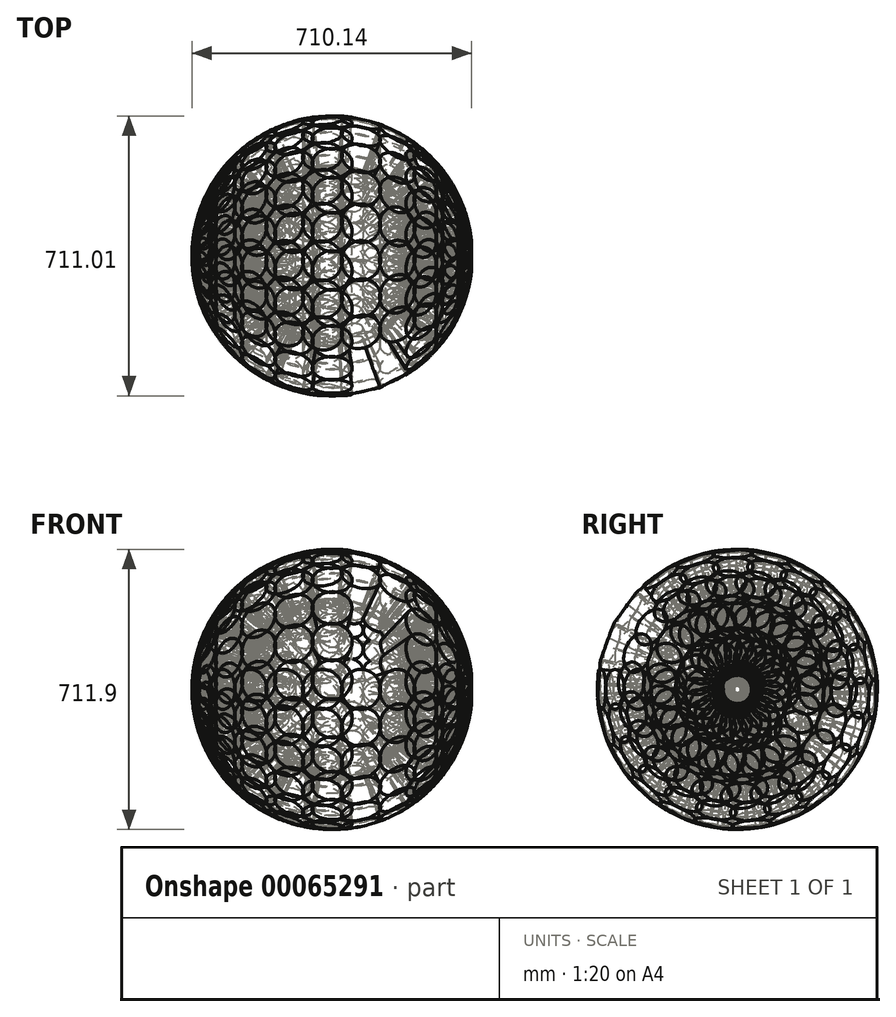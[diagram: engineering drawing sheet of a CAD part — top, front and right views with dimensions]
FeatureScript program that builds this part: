
annotation { "Feature Type Name" : "Feature", "Feature Type Description" : "" }
export const myFeature = defineFeature(function(context is Context, id is Id, definition is map)
    precondition{}
    {
        {
            var Q0;
            Q0=qCreatedBy(makeId("Top.planeOp"),FACE);
            var sketch = newSketch(context, id + "F4", { "sketchPlane" : qUnion([Q0])});
            skLineSegment(sketch, "E0", {"start": v(0, 228.6) * mm, "end": v(0, 352.43) * mm});
            skLineSegment(sketch, "E1", {"start": v(0, 352.43) * mm, "end": v(50.8, 352.43) * mm});
            skLineSegment(sketch, "E2", {"start": v(50.8, 352.43) * mm, "end": v(31.75, 228.6) * mm});
            skLineSegment(sketch, "E3", {"start": v(31.75, 228.6) * mm, "end": v(0, 228.6) * mm});
            skLineSegment(sketch, "E4", {"start": v(31.75, 228.6) * mm, "end": v(31.75, 352.43) * mm, "construction": true});
            skSolve(sketch);
        }
        {
            var Q0;
            Q0=makeQuery(id+"F4.imprint","IMPRINT",FACE,{"disambiguationData":[TD([[makeQuery(id+"F4.imprint","IMPRINT",EDGE,{"derivedFrom":sQuery(id+"F4.wireOp",EDGE,"E0")}),-1.0]])]});
            var Q1;
            Q1=sQuery(id+"F4.wireOp",EDGE,"E0");
            var Q2;
            Q2=sQuery(id+"F4.wireOp",EDGE,"E0");
            revolve(context, id + "F5", {"entities" : qUnion([Q0]), "surfaceEntities" : qUnion([Q1]), "axis" : qUnion([Q2]), "revolveType" : RevolveType.FULL});
        }
        {
            var Q0;
            Q0=qCreatedBy(makeId("Top.planeOp"),FACE);
            var sketch = newSketch(context, id + "F0", { "sketchPlane" : qUnion([Q0])});
            skCircle(sketch, "E5", {"center": v(0, 0) * mm, "radius": 228.6 * mm});
            skSolve(sketch);
        }
        {
            var Q0;
            Q0=makeQuery(id+"F5.opRevolve","SWEPT_BODY",BODY,{"disambiguationData":[OSD([sQuery(id+"F4.wireOp",EDGE,"E0"),sQuery(id+"F4.wireOp",EDGE,"E1"),sQuery(id+"F4.wireOp",EDGE,"E2"),sQuery(id+"F4.wireOp",EDGE,"E3")])]});
            var Q1;
            Q1=sQuery(id+"F0.wireOp",EDGE,"E5");
            circularPattern(context, id + "F1", {"operationType" : NewBodyOperationType.ADD, "entities" : qUnion([Q0]), "axis" : qUnion([Q1]), "angle" : 16 * degree, "instanceCount" : 21});
        }
        {
            var Q0;
            Q0=qCreatedBy(makeId("Right.planeOp"),FACE);
            var sketch = newSketch(context, id + "F2", { "sketchPlane" : qUnion([Q0])});
            skCircle(sketch, "E6", {"center": v(0, 0) * mm, "radius": 228.6 * mm});
            skSolve(sketch);
        }
        {
            var Q0;
            Q0=makeQuery(id+"F5.opRevolve","SWEPT_BODY",BODY,{"disambiguationData":[OSD([sQuery(id+"F4.wireOp",EDGE,"E0"),sQuery(id+"F4.wireOp",EDGE,"E1"),sQuery(id+"F4.wireOp",EDGE,"E2"),sQuery(id+"F4.wireOp",EDGE,"E3")])]});
            var Q1;
            Q1=sQuery(id+"F2.wireOp",EDGE,"E6");
            circularPattern(context, id + "F3", {"entities" : qUnion([Q0]), "axis" : qUnion([Q1]), "angle" : 16 * degree, "instanceCount" : 20});
        }
    });
